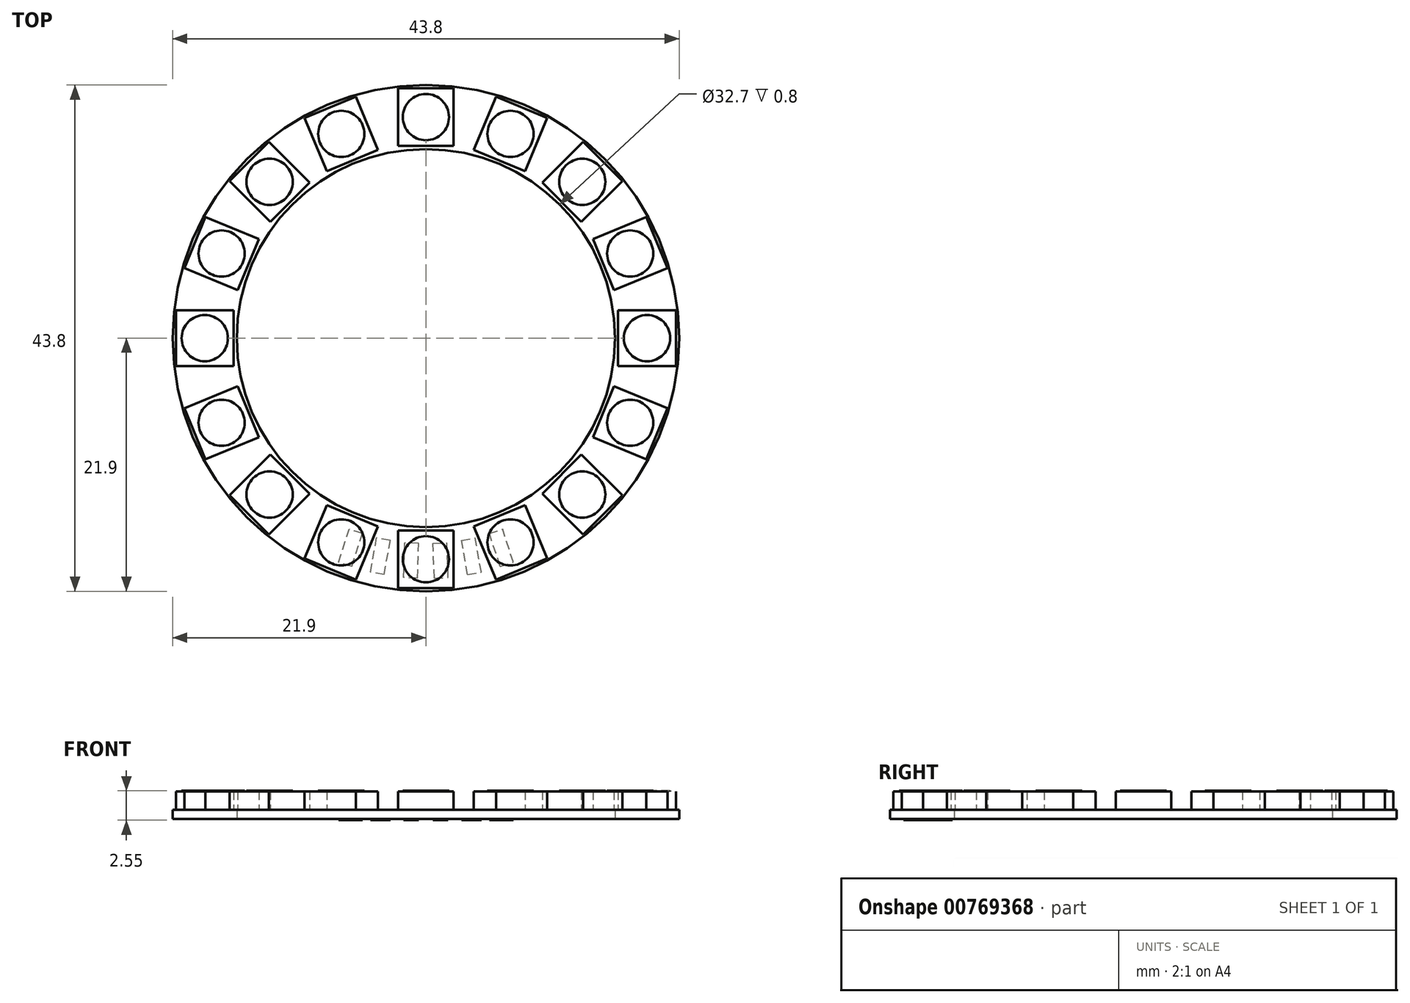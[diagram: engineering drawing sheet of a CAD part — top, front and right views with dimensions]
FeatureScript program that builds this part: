
annotation { "Feature Type Name" : "Feature", "Feature Type Description" : "" }
export const myFeature = defineFeature(function(context is Context, id is Id, definition is map)
    precondition{}
    {
        {
            var Q0;
            Q0=qCreatedBy(makeId("Top.planeOp"),FACE);
            var sketch = newSketch(context, id + "F0", { "sketchPlane" : qUnion([Q0])});
            skCircle(sketch, "E0", {"center": v(0, 0) * mm, "radius": 16.35 * mm});
            skCircle(sketch, "E1", {"center": v(0, 0) * mm, "radius": 21.9 * mm});
            skSolve(sketch);
        }
        {
            var Q0;
            Q0=makeQuery(id+"F0.imprint","IMPRINT",FACE,{"disambiguationData":[TD([[makeQuery(id+"F0.imprint","IMPRINT",EDGE,{"derivedFrom":sQuery(id+"F0.wireOp",EDGE,"E0")}),-1.0]])]});
            extrude(context, id + "F1", {"entities" : qUnion([Q0]), "depth" : 0.8 * mm});
        }
        {
            var Q0;
            Q0=makeQuery(id+"F1.opExtrude","CAP_FACE",FACE,{"disambiguationData":[OSD([sQuery(id+"F0.wireOp",EDGE,"E0"),sQuery(id+"F0.wireOp",EDGE,"E1")])],"isStart":false});
            var sketch = newSketch(context, id + "F2", { "sketchPlane" : qUnion([Q0])});
            skLineSegment(sketch, "E2", {"start": v(0, 21.9) * mm, "end": v(0, 16.35) * mm});
            skLineSegment(sketch, "E3.bottom", {"start": v(2.4, 16.62) * mm, "end": v(-2.4, 16.62) * mm});
            skLineSegment(sketch, "E3.top", {"start": v(2.4, 21.63) * mm, "end": v(-2.4, 21.63) * mm});
            skLineSegment(sketch, "E3.left", {"start": v(2.4, 16.62) * mm, "end": v(2.4, 21.63) * mm});
            skLineSegment(sketch, "E3.right", {"start": v(-2.4, 16.62) * mm, "end": v(-2.4, 21.63) * mm});
            skPoint(sketch, "E3.middle", {"position": v(0, 19.13) * mm});
            skLineSegment(sketch, "E4.1.0", {"start": v(-8.58, 14.44) * mm, "end": v(-10.5, 19.06) * mm});
            skLineSegment(sketch, "E4.1.1", {"start": v(-6.06, 20.9) * mm, "end": v(-10.5, 19.06) * mm});
            skLineSegment(sketch, "E4.1.2", {"start": v(-4.14, 16.28) * mm, "end": v(-6.06, 20.9) * mm});
            skLineSegment(sketch, "E4.1.3", {"start": v(-4.14, 16.28) * mm, "end": v(-8.58, 14.44) * mm});
            skLineSegment(sketch, "E4.2.0", {"start": v(-13.45, 10.06) * mm, "end": v(-16.99, 13.6) * mm});
            skLineSegment(sketch, "E4.2.1", {"start": v(-13.6, 16.99) * mm, "end": v(-16.99, 13.6) * mm});
            skLineSegment(sketch, "E4.2.2", {"start": v(-10.06, 13.45) * mm, "end": v(-13.6, 16.99) * mm});
            skLineSegment(sketch, "E4.2.3", {"start": v(-10.06, 13.45) * mm, "end": v(-13.45, 10.06) * mm});
            skLineSegment(sketch, "E4.3.0", {"start": v(-16.28, 4.14) * mm, "end": v(-20.9, 6.06) * mm});
            skLineSegment(sketch, "E4.3.1", {"start": v(-19.06, 10.5) * mm, "end": v(-20.9, 6.06) * mm});
            skLineSegment(sketch, "E4.3.2", {"start": v(-14.44, 8.58) * mm, "end": v(-19.06, 10.5) * mm});
            skLineSegment(sketch, "E4.3.3", {"start": v(-14.44, 8.58) * mm, "end": v(-16.28, 4.14) * mm});
            skLineSegment(sketch, "E4.4.0", {"start": v(-16.62, -2.4) * mm, "end": v(-21.63, -2.4) * mm});
            skLineSegment(sketch, "E4.4.1", {"start": v(-21.63, 2.4) * mm, "end": v(-21.63, -2.4) * mm});
            skLineSegment(sketch, "E4.4.2", {"start": v(-16.62, 2.4) * mm, "end": v(-21.63, 2.4) * mm});
            skLineSegment(sketch, "E4.4.3", {"start": v(-16.62, 2.4) * mm, "end": v(-16.62, -2.4) * mm});
            skLineSegment(sketch, "E4.5.0", {"start": v(-14.44, -8.58) * mm, "end": v(-19.06, -10.5) * mm});
            skLineSegment(sketch, "E4.5.1", {"start": v(-20.9, -6.06) * mm, "end": v(-19.06, -10.5) * mm});
            skLineSegment(sketch, "E4.5.2", {"start": v(-16.28, -4.14) * mm, "end": v(-20.9, -6.06) * mm});
            skLineSegment(sketch, "E4.5.3", {"start": v(-16.28, -4.14) * mm, "end": v(-14.44, -8.58) * mm});
            skLineSegment(sketch, "E4.6.0", {"start": v(-10.06, -13.45) * mm, "end": v(-13.6, -16.99) * mm});
            skLineSegment(sketch, "E4.6.1", {"start": v(-16.99, -13.6) * mm, "end": v(-13.6, -16.99) * mm});
            skLineSegment(sketch, "E4.6.2", {"start": v(-13.45, -10.06) * mm, "end": v(-16.99, -13.6) * mm});
            skLineSegment(sketch, "E4.6.3", {"start": v(-13.45, -10.06) * mm, "end": v(-10.06, -13.45) * mm});
            skLineSegment(sketch, "E4.7.0", {"start": v(-4.14, -16.28) * mm, "end": v(-6.06, -20.9) * mm});
            skLineSegment(sketch, "E4.7.1", {"start": v(-10.5, -19.06) * mm, "end": v(-6.06, -20.9) * mm});
            skLineSegment(sketch, "E4.7.2", {"start": v(-8.58, -14.44) * mm, "end": v(-10.5, -19.06) * mm});
            skLineSegment(sketch, "E4.7.3", {"start": v(-8.58, -14.44) * mm, "end": v(-4.14, -16.28) * mm});
            skLineSegment(sketch, "E4.8.0", {"start": v(2.4, -16.62) * mm, "end": v(2.4, -21.63) * mm});
            skLineSegment(sketch, "E4.8.1", {"start": v(-2.4, -21.63) * mm, "end": v(2.4, -21.63) * mm});
            skLineSegment(sketch, "E4.8.2", {"start": v(-2.4, -16.62) * mm, "end": v(-2.4, -21.63) * mm});
            skLineSegment(sketch, "E4.8.3", {"start": v(-2.4, -16.62) * mm, "end": v(2.4, -16.62) * mm});
            skLineSegment(sketch, "E4.9.0", {"start": v(8.58, -14.44) * mm, "end": v(10.5, -19.06) * mm});
            skLineSegment(sketch, "E4.9.1", {"start": v(6.06, -20.9) * mm, "end": v(10.5, -19.06) * mm});
            skLineSegment(sketch, "E4.9.2", {"start": v(4.14, -16.28) * mm, "end": v(6.06, -20.9) * mm});
            skLineSegment(sketch, "E4.9.3", {"start": v(4.14, -16.28) * mm, "end": v(8.58, -14.44) * mm});
            skLineSegment(sketch, "E4.10.0", {"start": v(13.45, -10.06) * mm, "end": v(16.99, -13.6) * mm});
            skLineSegment(sketch, "E4.10.1", {"start": v(13.6, -16.99) * mm, "end": v(16.99, -13.6) * mm});
            skLineSegment(sketch, "E4.10.2", {"start": v(10.06, -13.45) * mm, "end": v(13.6, -16.99) * mm});
            skLineSegment(sketch, "E4.10.3", {"start": v(10.06, -13.45) * mm, "end": v(13.45, -10.06) * mm});
            skLineSegment(sketch, "E4.11.0", {"start": v(16.28, -4.14) * mm, "end": v(20.9, -6.06) * mm});
            skLineSegment(sketch, "E4.11.1", {"start": v(19.06, -10.5) * mm, "end": v(20.9, -6.06) * mm});
            skLineSegment(sketch, "E4.11.2", {"start": v(14.44, -8.58) * mm, "end": v(19.06, -10.5) * mm});
            skLineSegment(sketch, "E4.11.3", {"start": v(14.44, -8.58) * mm, "end": v(16.28, -4.14) * mm});
            skLineSegment(sketch, "E4.12.0", {"start": v(16.62, 2.4) * mm, "end": v(21.63, 2.4) * mm});
            skLineSegment(sketch, "E4.12.1", {"start": v(21.63, -2.4) * mm, "end": v(21.63, 2.4) * mm});
            skLineSegment(sketch, "E4.12.2", {"start": v(16.62, -2.4) * mm, "end": v(21.63, -2.4) * mm});
            skLineSegment(sketch, "E4.12.3", {"start": v(16.62, -2.4) * mm, "end": v(16.62, 2.4) * mm});
            skLineSegment(sketch, "E4.13.0", {"start": v(14.44, 8.58) * mm, "end": v(19.06, 10.5) * mm});
            skLineSegment(sketch, "E4.13.1", {"start": v(20.9, 6.06) * mm, "end": v(19.06, 10.5) * mm});
            skLineSegment(sketch, "E4.13.2", {"start": v(16.28, 4.14) * mm, "end": v(20.9, 6.06) * mm});
            skLineSegment(sketch, "E4.13.3", {"start": v(16.28, 4.14) * mm, "end": v(14.44, 8.58) * mm});
            skLineSegment(sketch, "E4.14.0", {"start": v(10.06, 13.45) * mm, "end": v(13.6, 16.99) * mm});
            skLineSegment(sketch, "E4.14.1", {"start": v(16.99, 13.6) * mm, "end": v(13.6, 16.99) * mm});
            skLineSegment(sketch, "E4.14.2", {"start": v(13.45, 10.06) * mm, "end": v(16.99, 13.6) * mm});
            skLineSegment(sketch, "E4.14.3", {"start": v(13.45, 10.06) * mm, "end": v(10.06, 13.45) * mm});
            skLineSegment(sketch, "E4.15.0", {"start": v(4.14, 16.28) * mm, "end": v(6.06, 20.9) * mm});
            skLineSegment(sketch, "E4.15.1", {"start": v(10.5, 19.06) * mm, "end": v(6.06, 20.9) * mm});
            skLineSegment(sketch, "E4.15.2", {"start": v(8.58, 14.44) * mm, "end": v(10.5, 19.06) * mm});
            skLineSegment(sketch, "E4.15.3", {"start": v(8.58, 14.44) * mm, "end": v(4.14, 16.28) * mm});
            skPoint(sketch, "E4.center", {"position": v(0, 0) * mm});
            skCircle(sketch, "E5", {"center": v(0, 19.13) * mm, "radius": 2 * mm});
            skCircle(sketch, "E6.1.0", {"center": v(-7.32, 17.67) * mm, "radius": 2 * mm});
            skCircle(sketch, "E6.2.0", {"center": v(-13.52, 13.52) * mm, "radius": 2 * mm});
            skCircle(sketch, "E6.3.0", {"center": v(-17.67, 7.32) * mm, "radius": 2 * mm});
            skCircle(sketch, "E6.4.0", {"center": v(-19.13, 0) * mm, "radius": 2 * mm});
            skCircle(sketch, "E6.5.0", {"center": v(-17.67, -7.32) * mm, "radius": 2 * mm});
            skCircle(sketch, "E6.6.0", {"center": v(-13.52, -13.52) * mm, "radius": 2 * mm});
            skCircle(sketch, "E6.7.0", {"center": v(-7.32, -17.67) * mm, "radius": 2 * mm});
            skCircle(sketch, "E6.8.0", {"center": v(0, -19.13) * mm, "radius": 2 * mm});
            skCircle(sketch, "E6.9.0", {"center": v(7.32, -17.67) * mm, "radius": 2 * mm});
            skCircle(sketch, "E6.10.0", {"center": v(13.52, -13.52) * mm, "radius": 2 * mm});
            skCircle(sketch, "E6.11.0", {"center": v(17.67, -7.32) * mm, "radius": 2 * mm});
            skCircle(sketch, "E6.12.0", {"center": v(19.13, 0) * mm, "radius": 2 * mm});
            skCircle(sketch, "E6.13.0", {"center": v(17.67, 7.32) * mm, "radius": 2 * mm});
            skCircle(sketch, "E6.14.0", {"center": v(13.52, 13.52) * mm, "radius": 2 * mm});
            skCircle(sketch, "E6.15.0", {"center": v(7.32, 17.67) * mm, "radius": 2 * mm});
            skSolve(sketch);
        }
        {
            var Q0;
            Q0=qSketchRegion(id+"F2",true);
            extrude(context, id + "F3", {"entities" : qUnion([Q0]), "operationType" : NewBodyOperationType.ADD, "depth" : 1.6 * mm});
        }
        {
            var Q0;
            Q0=makeQuery(id+"F3.boolean.opBoolean","SPLIT",FACE,{"disambiguationData":[TD([makeQuery(id+"F3.opExtrude","SWEPT_FACE",FACE,{"disambiguationData":[OSD([sQuery(id+"F2.wireOp",EDGE,"E6.3.0")])]})])],"derivedFrom":makeQuery(id+"F1.opExtrude","CAP_FACE",FACE,{"disambiguationData":[OSD([sQuery(id+"F0.wireOp",EDGE,"E0"),sQuery(id+"F0.wireOp",EDGE,"E1")])],"isStart":false})});
            var Q1;
            Q1=makeQuery(id+"F3.boolean.opBoolean","SPLIT",FACE,{"disambiguationData":[TD([makeQuery(id+"F3.opExtrude","SWEPT_FACE",FACE,{"disambiguationData":[OSD([sQuery(id+"F2.wireOp",EDGE,"E6.2.0")])]})])],"derivedFrom":makeQuery(id+"F1.opExtrude","CAP_FACE",FACE,{"disambiguationData":[OSD([sQuery(id+"F0.wireOp",EDGE,"E0"),sQuery(id+"F0.wireOp",EDGE,"E1")])],"isStart":false})});
            var Q2;
            Q2=makeQuery(id+"F3.boolean.opBoolean","SPLIT",FACE,{"disambiguationData":[TD([makeQuery(id+"F3.opExtrude","SWEPT_FACE",FACE,{"disambiguationData":[OSD([sQuery(id+"F2.wireOp",EDGE,"E6.1.0")])]})])],"derivedFrom":makeQuery(id+"F1.opExtrude","CAP_FACE",FACE,{"disambiguationData":[OSD([sQuery(id+"F0.wireOp",EDGE,"E0"),sQuery(id+"F0.wireOp",EDGE,"E1")])],"isStart":false})});
            var Q3;
            Q3=makeQuery(id+"F3.boolean.opBoolean","SPLIT",FACE,{"disambiguationData":[TD([makeQuery(id+"F3.opExtrude","SWEPT_FACE",FACE,{"disambiguationData":[OSD([sQuery(id+"F2.wireOp",EDGE,"E5")])]})])],"derivedFrom":makeQuery(id+"F1.opExtrude","CAP_FACE",FACE,{"disambiguationData":[OSD([sQuery(id+"F0.wireOp",EDGE,"E0"),sQuery(id+"F0.wireOp",EDGE,"E1")])],"isStart":false})});
            var Q4;
            Q4=makeQuery(id+"F3.boolean.opBoolean","SPLIT",FACE,{"disambiguationData":[TD([makeQuery(id+"F3.opExtrude","SWEPT_FACE",FACE,{"disambiguationData":[OSD([sQuery(id+"F2.wireOp",EDGE,"E6.15.0")])]})])],"derivedFrom":makeQuery(id+"F1.opExtrude","CAP_FACE",FACE,{"disambiguationData":[OSD([sQuery(id+"F0.wireOp",EDGE,"E0"),sQuery(id+"F0.wireOp",EDGE,"E1")])],"isStart":false})});
            var Q5;
            Q5=makeQuery(id+"F3.boolean.opBoolean","SPLIT",FACE,{"disambiguationData":[TD([makeQuery(id+"F3.opExtrude","SWEPT_FACE",FACE,{"disambiguationData":[OSD([sQuery(id+"F2.wireOp",EDGE,"E6.4.0")])]})])],"derivedFrom":makeQuery(id+"F1.opExtrude","CAP_FACE",FACE,{"disambiguationData":[OSD([sQuery(id+"F0.wireOp",EDGE,"E0"),sQuery(id+"F0.wireOp",EDGE,"E1")])],"isStart":false})});
            var Q6;
            Q6=makeQuery(id+"F3.boolean.opBoolean","SPLIT",FACE,{"disambiguationData":[TD([makeQuery(id+"F3.opExtrude","SWEPT_FACE",FACE,{"disambiguationData":[OSD([sQuery(id+"F2.wireOp",EDGE,"E6.5.0")])]})])],"derivedFrom":makeQuery(id+"F1.opExtrude","CAP_FACE",FACE,{"disambiguationData":[OSD([sQuery(id+"F0.wireOp",EDGE,"E0"),sQuery(id+"F0.wireOp",EDGE,"E1")])],"isStart":false})});
            var Q7;
            Q7=makeQuery(id+"F3.boolean.opBoolean","SPLIT",FACE,{"disambiguationData":[TD([makeQuery(id+"F3.opExtrude","SWEPT_FACE",FACE,{"disambiguationData":[OSD([sQuery(id+"F2.wireOp",EDGE,"E6.6.0")])]})])],"derivedFrom":makeQuery(id+"F1.opExtrude","CAP_FACE",FACE,{"disambiguationData":[OSD([sQuery(id+"F0.wireOp",EDGE,"E0"),sQuery(id+"F0.wireOp",EDGE,"E1")])],"isStart":false})});
            var Q8;
            Q8=makeQuery(id+"F3.boolean.opBoolean","SPLIT",FACE,{"disambiguationData":[TD([makeQuery(id+"F3.opExtrude","SWEPT_FACE",FACE,{"disambiguationData":[OSD([sQuery(id+"F2.wireOp",EDGE,"E6.7.0")])]})])],"derivedFrom":makeQuery(id+"F1.opExtrude","CAP_FACE",FACE,{"disambiguationData":[OSD([sQuery(id+"F0.wireOp",EDGE,"E0"),sQuery(id+"F0.wireOp",EDGE,"E1")])],"isStart":false})});
            var Q9;
            Q9=makeQuery(id+"F3.boolean.opBoolean","SPLIT",FACE,{"disambiguationData":[TD([makeQuery(id+"F3.opExtrude","SWEPT_FACE",FACE,{"disambiguationData":[OSD([sQuery(id+"F2.wireOp",EDGE,"E6.8.0")])]})])],"derivedFrom":makeQuery(id+"F1.opExtrude","CAP_FACE",FACE,{"disambiguationData":[OSD([sQuery(id+"F0.wireOp",EDGE,"E0"),sQuery(id+"F0.wireOp",EDGE,"E1")])],"isStart":false})});
            var Q10;
            Q10=makeQuery(id+"F3.boolean.opBoolean","SPLIT",FACE,{"disambiguationData":[TD([makeQuery(id+"F3.opExtrude","SWEPT_FACE",FACE,{"disambiguationData":[OSD([sQuery(id+"F2.wireOp",EDGE,"E6.9.0")])]})])],"derivedFrom":makeQuery(id+"F1.opExtrude","CAP_FACE",FACE,{"disambiguationData":[OSD([sQuery(id+"F0.wireOp",EDGE,"E0"),sQuery(id+"F0.wireOp",EDGE,"E1")])],"isStart":false})});
            var Q11;
            Q11=makeQuery(id+"F3.boolean.opBoolean","SPLIT",FACE,{"disambiguationData":[TD([makeQuery(id+"F3.opExtrude","SWEPT_FACE",FACE,{"disambiguationData":[OSD([sQuery(id+"F2.wireOp",EDGE,"E6.10.0")])]})])],"derivedFrom":makeQuery(id+"F1.opExtrude","CAP_FACE",FACE,{"disambiguationData":[OSD([sQuery(id+"F0.wireOp",EDGE,"E0"),sQuery(id+"F0.wireOp",EDGE,"E1")])],"isStart":false})});
            var Q12;
            Q12=makeQuery(id+"F3.boolean.opBoolean","SPLIT",FACE,{"disambiguationData":[TD([makeQuery(id+"F3.opExtrude","SWEPT_FACE",FACE,{"disambiguationData":[OSD([sQuery(id+"F2.wireOp",EDGE,"E6.11.0")])]})])],"derivedFrom":makeQuery(id+"F1.opExtrude","CAP_FACE",FACE,{"disambiguationData":[OSD([sQuery(id+"F0.wireOp",EDGE,"E0"),sQuery(id+"F0.wireOp",EDGE,"E1")])],"isStart":false})});
            var Q13;
            Q13=makeQuery(id+"F3.boolean.opBoolean","SPLIT",FACE,{"disambiguationData":[TD([makeQuery(id+"F3.opExtrude","SWEPT_FACE",FACE,{"disambiguationData":[OSD([sQuery(id+"F2.wireOp",EDGE,"E6.12.0")])]})])],"derivedFrom":makeQuery(id+"F1.opExtrude","CAP_FACE",FACE,{"disambiguationData":[OSD([sQuery(id+"F0.wireOp",EDGE,"E0"),sQuery(id+"F0.wireOp",EDGE,"E1")])],"isStart":false})});
            var Q14;
            Q14=makeQuery(id+"F3.boolean.opBoolean","SPLIT",FACE,{"disambiguationData":[TD([makeQuery(id+"F3.opExtrude","SWEPT_FACE",FACE,{"disambiguationData":[OSD([sQuery(id+"F2.wireOp",EDGE,"E6.14.0")])]})])],"derivedFrom":makeQuery(id+"F1.opExtrude","CAP_FACE",FACE,{"disambiguationData":[OSD([sQuery(id+"F0.wireOp",EDGE,"E0"),sQuery(id+"F0.wireOp",EDGE,"E1")])],"isStart":false})});
            var Q15;
            Q15=makeQuery(id+"F3.boolean.opBoolean","SPLIT",FACE,{"disambiguationData":[TD([makeQuery(id+"F3.opExtrude","SWEPT_FACE",FACE,{"disambiguationData":[OSD([sQuery(id+"F2.wireOp",EDGE,"E6.13.0")])]})])],"derivedFrom":makeQuery(id+"F1.opExtrude","CAP_FACE",FACE,{"disambiguationData":[OSD([sQuery(id+"F0.wireOp",EDGE,"E0"),sQuery(id+"F0.wireOp",EDGE,"E1")])],"isStart":false})});
            extrude(context, id + "F4", {"entities" : qUnion([Q0, Q1, Q2, Q3, Q4, Q5, Q6, Q7, Q8, Q9, Q10, Q11, Q12, Q13, Q14, Q15]), "operationType" : NewBodyOperationType.ADD, "depth" : 1.65 * mm});
        }
        {
            var Q0;
            Q0=makeQuery(id+"F1.opExtrude","CAP_FACE",FACE,{"disambiguationData":[OSD([sQuery(id+"F0.wireOp",EDGE,"E0"),sQuery(id+"F0.wireOp",EDGE,"E1")])],"isStart":true});
            var sketch = newSketch(context, id + "F5", { "sketchPlane" : qUnion([Q0])});
            skLineSegment(sketch, "E7", {"start": v(0, 0) * mm, "end": v(5.49, 16.9) * mm, "construction": true});
            skLineSegment(sketch, "E8.bottom", {"start": v(6.42, 19.75) * mm, "end": v(7.56, 19.38) * mm});
            skLineSegment(sketch, "E8.top", {"start": v(5.49, 16.9) * mm, "end": v(6.63, 16.52) * mm});
            skLineSegment(sketch, "E8.left", {"start": v(6.42, 19.75) * mm, "end": v(5.49, 16.9) * mm});
            skLineSegment(sketch, "E8.right", {"start": v(7.56, 19.38) * mm, "end": v(6.63, 16.52) * mm});
            skLineSegment(sketch, "E9", {"start": v(0, 0) * mm, "end": v(0.62, 17.75) * mm, "construction": true});
            skLineSegment(sketch, "E10.bottom", {"start": v(0.72, 20.75) * mm, "end": v(1.92, 20.7) * mm});
            skLineSegment(sketch, "E10.top", {"start": v(0.62, 17.75) * mm, "end": v(1.82, 17.71) * mm});
            skLineSegment(sketch, "E10.left", {"start": v(0.72, 20.75) * mm, "end": v(0.62, 17.75) * mm});
            skLineSegment(sketch, "E10.right", {"start": v(1.92, 20.7) * mm, "end": v(1.82, 17.71) * mm});
            skLineSegment(sketch, "E11", {"start": v(0, 0) * mm, "end": v(3.08, 17.5) * mm, "construction": true});
            skLineSegment(sketch, "E12.bottom", {"start": v(3.6, 20.45) * mm, "end": v(4.79, 20.24) * mm});
            skLineSegment(sketch, "E12.top", {"start": v(3.08, 17.5) * mm, "end": v(4.27, 17.29) * mm});
            skLineSegment(sketch, "E12.left", {"start": v(3.6, 20.45) * mm, "end": v(3.08, 17.5) * mm});
            skLineSegment(sketch, "E12.right", {"start": v(4.79, 20.24) * mm, "end": v(4.27, 17.29) * mm});
            skLineSegment(sketch, "E13.MirrorCS", {"start": v(-0.72, 20.75) * mm, "end": v(-1.92, 20.7) * mm});
            skLineSegment(sketch, "E14.MirrorCS", {"start": v(-0.62, 17.75) * mm, "end": v(-1.82, 17.71) * mm});
            skLineSegment(sketch, "E15.MirrorCS", {"start": v(-1.92, 20.7) * mm, "end": v(-1.82, 17.71) * mm});
            skLineSegment(sketch, "E16.MirrorCS", {"start": v(0, 0) * mm, "end": v(-0.62, 17.75) * mm, "construction": true});
            skLineSegment(sketch, "E17.MirrorCS", {"start": v(-3.6, 20.45) * mm, "end": v(-4.79, 20.24) * mm});
            skLineSegment(sketch, "E18.MirrorCS", {"start": v(-4.79, 20.24) * mm, "end": v(-4.27, 17.29) * mm});
            skLineSegment(sketch, "E19.MirrorCS", {"start": v(-3.08, 17.5) * mm, "end": v(-4.27, 17.29) * mm});
            skLineSegment(sketch, "E20.MirrorCS", {"start": v(-6.42, 19.75) * mm, "end": v(-7.56, 19.38) * mm});
            skLineSegment(sketch, "E21.MirrorCS", {"start": v(-7.56, 19.38) * mm, "end": v(-6.63, 16.52) * mm});
            skLineSegment(sketch, "E22.MirrorCS", {"start": v(-5.49, 16.9) * mm, "end": v(-6.63, 16.52) * mm});
            skLineSegment(sketch, "E23.MirrorCS", {"start": v(-6.42, 19.75) * mm, "end": v(-5.49, 16.9) * mm});
            skLineSegment(sketch, "E24.MirrorCS", {"start": v(-3.6, 20.45) * mm, "end": v(-3.08, 17.5) * mm});
            skLineSegment(sketch, "E25.MirrorCS", {"start": v(-0.72, 20.75) * mm, "end": v(-0.62, 17.75) * mm});
            skSolve(sketch);
        }
        {
            var Q0;
            Q0=qSketchRegion(id+"F5",true);
            extrude(context, id + "F6", {"entities" : qUnion([Q0]), "operationType" : NewBodyOperationType.ADD, "depth" : .1 * mm});
        }
    });
